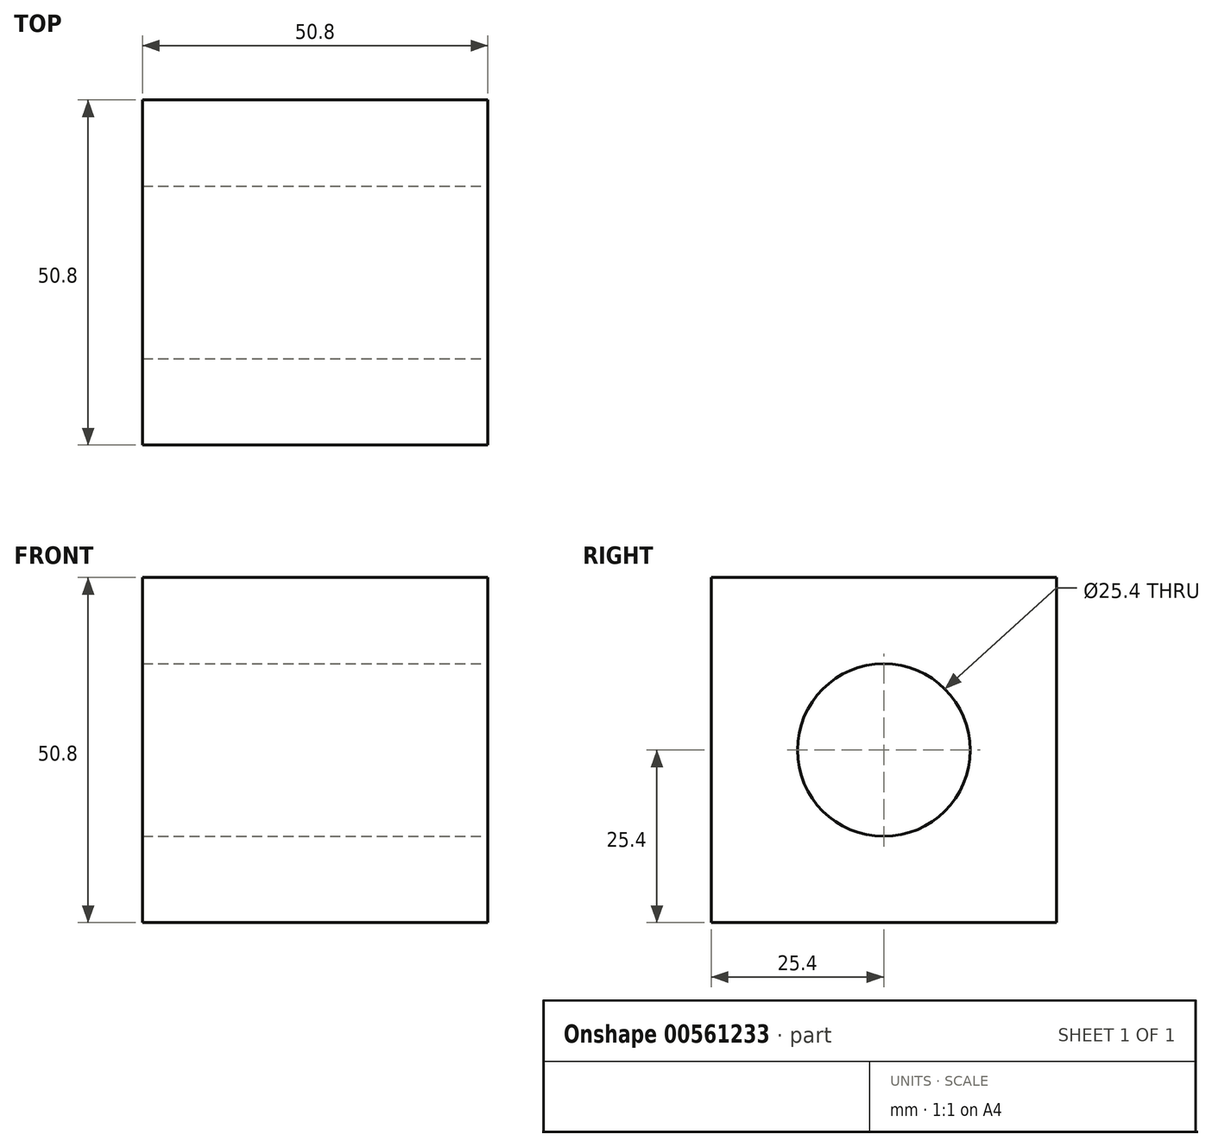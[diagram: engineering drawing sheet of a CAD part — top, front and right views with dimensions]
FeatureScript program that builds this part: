
annotation { "Feature Type Name" : "Feature", "Feature Type Description" : "" }
export const myFeature = defineFeature(function(context is Context, id is Id, definition is map)
    precondition{}
    {
        {
            var Q0;
            Q0=qCreatedBy(makeId("Top.planeOp"),FACE);
            var sketch = newSketch(context, id + "F0", { "sketchPlane" : qUnion([Q0])});
            skLineSegment(sketch, "E0.bottom", {"start": v(0, 0) * mm, "end": v(50.8, 0) * mm});
            skLineSegment(sketch, "E0.top", {"start": v(0, 50.8) * mm, "end": v(50.8, 50.8) * mm});
            skLineSegment(sketch, "E0.left", {"start": v(0, 0) * mm, "end": v(0, 50.8) * mm});
            skLineSegment(sketch, "E0.right", {"start": v(50.8, 0) * mm, "end": v(50.8, 50.8) * mm});
            skSolve(sketch);
        }
        {
            var Q0;
            Q0=makeQuery(id+"F0.imprint","IMPRINT",FACE,{"disambiguationData":[TD([[makeQuery(id+"F0.imprint","IMPRINT",EDGE,{"derivedFrom":sQuery(id+"F0.wireOp",EDGE,"E0.bottom")}),1.0]])]});
            extrude(context, id + "F1", {"entities" : qUnion([Q0]), "depth" : 50.8 * mm, "offsetDistance" : 25.4 * mm});
        }
        {
            var Q0;
            Q0=makeQuery(id+"F1.opExtrude","SWEPT_FACE",FACE,{"disambiguationData":[OSD([sQuery(id+"F0.wireOp",EDGE,"E0.right")])]});
            var sketch = newSketch(context, id + "F2", { "sketchPlane" : qUnion([Q0])});
            skCircle(sketch, "E1", {"center": v(25.4, 25.4) * mm, "radius": 12.7 * mm});
            skPoint(sketch, "E1.centerSnap0", {"position": v(0, 25.4) * mm});
            skPoint(sketch, "E1.centerSnap1", {"position": v(25.4, 0) * mm});
            skSolve(sketch);
        }
        {
            var Q0;
            Q0=makeQuery(id+"F2.imprint","IMPRINT",FACE,{"disambiguationData":[TD([[makeQuery(id+"F2.imprint","IMPRINT",EDGE,{"derivedFrom":sQuery(id+"F2.wireOp",EDGE,"E1")}),1.0]])]});
            extrude(context, id + "F3", {"entities" : qUnion([Q0]), "operationType" : NewBodyOperationType.REMOVE, "oppositeDirection" : true, "depth" : 50.8 * mm, "offsetDistance" : 25.4 * mm});
        }
    });
